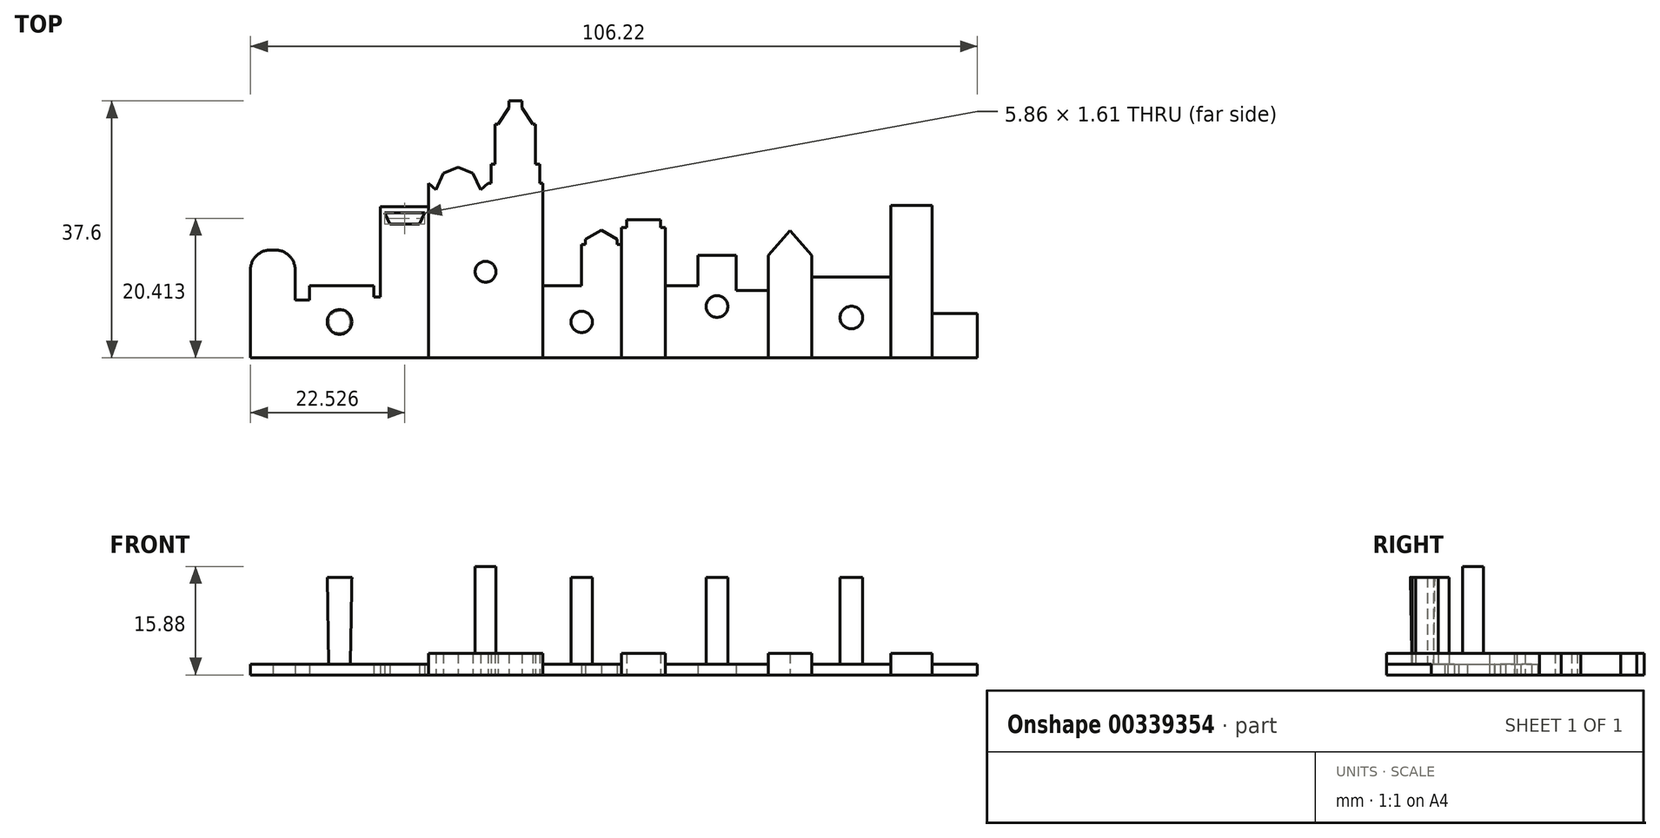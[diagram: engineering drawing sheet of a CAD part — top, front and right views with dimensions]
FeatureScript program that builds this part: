
annotation { "Feature Type Name" : "Feature", "Feature Type Description" : "" }
export const myFeature = defineFeature(function(context is Context, id is Id, definition is map)
    precondition{}
    {
        {
            var Q0;
            Q0=qCreatedBy(makeId("Top.planeOp"),FACE);
            var sketch = newSketch(context, id + "F0", { "sketchPlane" : qUnion([Q0])});
            skLineSegment(sketch, "E0.bottom", {"start": v(0, 0) * mm, "end": v(6.51, 0) * mm});
            skLineSegment(sketch, "E0.top", {"start": v(2.85, 12.93) * mm, "end": v(3.26, 12.93) * mm});
            skLineSegment(sketch, "E0.left", {"start": v(0, 0) * mm, "end": v(0, 12.93) * mm});
            skLineSegment(sketch, "E0.right", {"start": v(6.51, 8.46) * mm, "end": v(6.51, 12.93) * mm});
            skLineSegment(sketch, "E1.bottom", {"start": v(5.34, 0) * mm, "end": v(8.63, 0) * mm});
            skLineSegment(sketch, "E1.top", {"start": v(6.51, 8.46) * mm, "end": v(8.63, 8.46) * mm});
            skLineSegment(sketch, "E2.bottom", {"start": v(8.63, 0) * mm, "end": v(18.03, 0) * mm});
            skLineSegment(sketch, "E2.top", {"start": v(8.63, 10.55) * mm, "end": v(18.03, 10.55) * mm});
            skLineSegment(sketch, "E2.left", {"start": v(8.63, 8.46) * mm, "end": v(8.63, 10.55) * mm});
            skLineSegment(sketch, "E2.right", {"start": v(18.03, 8.93) * mm, "end": v(18.03, 10.55) * mm});
            skLineSegment(sketch, "E3.bottom", {"start": v(16.62, 0) * mm, "end": v(18.97, 0) * mm});
            skLineSegment(sketch, "E3.top", {"start": v(18.03, 8.93) * mm, "end": v(18.97, 8.93) * mm});
            skLineSegment(sketch, "E4.bottom", {"start": v(18.97, 0) * mm, "end": v(26.02, 0) * mm});
            skLineSegment(sketch, "E4.top", {"start": v(18.97, 22.1) * mm, "end": v(26.02, 22.1) * mm});
            skLineSegment(sketch, "E4.left", {"start": v(18.97, 8.93) * mm, "end": v(18.97, 22.1) * mm});
            skLineSegment(sketch, "E4.right", {"start": v(26.02, 0) * mm, "end": v(26.02, 22.1) * mm});
            skLineSegment(sketch, "E5.bottom", {"start": v(26.02, 0) * mm, "end": v(34.71, 0) * mm});
            skLineSegment(sketch, "E5.left", {"start": v(26.02, 0) * mm, "end": v(26.02, 25.53) * mm});
            skLineSegment(sketch, "E5.right", {"start": v(34.71, 0) * mm, "end": v(34.71, 25.53) * mm});
            skLineSegment(sketch, "E6.bottom", {"start": v(34.71, 0) * mm, "end": v(42.7, 0) * mm});
            skLineSegment(sketch, "E6.top", {"start": v(37.76, 37.6) * mm, "end": v(39.65, 37.6) * mm});
            skLineSegment(sketch, "E6.right", {"start": v(42.7, 0) * mm, "end": v(42.7, 25.53) * mm});
            skLineSegment(sketch, "E7.bottom", {"start": v(42.7, 10.55) * mm, "end": v(48.34, 10.55) * mm});
            skLineSegment(sketch, "E7.top", {"start": v(42.7, 0) * mm, "end": v(48.34, 0) * mm});
            skLineSegment(sketch, "E7.left", {"start": v(42.7, 10.55) * mm, "end": v(42.7, 0) * mm});
            skLineSegment(sketch, "E7.right", {"start": v(48.34, 10.55) * mm, "end": v(48.34, 0) * mm});
            skLineSegment(sketch, "E8.bottom", {"start": v(48.34, 0) * mm, "end": v(54.22, 0) * mm});
            skLineSegment(sketch, "E8.left", {"start": v(48.34, 0) * mm, "end": v(48.34, 15.04) * mm});
            skLineSegment(sketch, "E8.right", {"start": v(54.22, 0) * mm, "end": v(54.22, 15.04) * mm});
            skLineSegment(sketch, "E9.top", {"start": v(54.97, 20.21) * mm, "end": v(59.9, 20.21) * mm});
            skLineSegment(sketch, "E9.left", {"start": v(54.22, 15.04) * mm, "end": v(54.22, 19.05) * mm});
            skLineSegment(sketch, "E9.right", {"start": v(60.66, 15.04) * mm, "end": v(60.66, 19.05) * mm});
            skLineSegment(sketch, "E10.top", {"start": v(60.66, 0) * mm, "end": v(54.22, 0) * mm});
            skLineSegment(sketch, "E10.left", {"start": v(60.66, 15.04) * mm, "end": v(60.66, 0) * mm});
            skLineSegment(sketch, "E10.right", {"start": v(54.22, 15.04) * mm, "end": v(54.22, 0) * mm});
            skLineSegment(sketch, "E11.bottom", {"start": v(60.66, 10.55) * mm, "end": v(65.36, 10.55) * mm});
            skLineSegment(sketch, "E11.top", {"start": v(60.66, 0) * mm, "end": v(65.36, 0) * mm});
            skLineSegment(sketch, "E11.left", {"start": v(60.66, 10.55) * mm, "end": v(60.66, 0) * mm});
            skLineSegment(sketch, "E11.right", {"start": v(65.36, 10.55) * mm, "end": v(65.36, 0) * mm});
            skLineSegment(sketch, "E12.bottom", {"start": v(65.36, 0) * mm, "end": v(71, 0) * mm});
            skLineSegment(sketch, "E12.top", {"start": v(65.36, 15.04) * mm, "end": v(71, 15.04) * mm});
            skLineSegment(sketch, "E12.left", {"start": v(65.36, 0) * mm, "end": v(65.36, 15.04) * mm});
            skLineSegment(sketch, "E12.right", {"start": v(71, 0) * mm, "end": v(71, 15.04) * mm});
            skLineSegment(sketch, "E13.bottom", {"start": v(71, 9.87) * mm, "end": v(75.7, 9.87) * mm});
            skLineSegment(sketch, "E13.top", {"start": v(71, 0) * mm, "end": v(75.7, 0) * mm});
            skLineSegment(sketch, "E13.left", {"start": v(71, 9.87) * mm, "end": v(71, 0) * mm});
            skLineSegment(sketch, "E13.right", {"start": v(75.7, 9.87) * mm, "end": v(75.7, 0) * mm});
            skLineSegment(sketch, "E14.bottom", {"start": v(75.7, 0) * mm, "end": v(82.05, 0) * mm});
            skLineSegment(sketch, "E14.left", {"start": v(75.7, 0) * mm, "end": v(75.7, 15.04) * mm});
            skLineSegment(sketch, "E14.right", {"start": v(82.05, 0) * mm, "end": v(82.05, 15.04) * mm});
            skArc(sketch, "E15", {"start": v(3.26, 15.75) * mm, "mid": v(0.98, 15.08) * mm, "end": v(0, 12.93) * mm});
            skPoint(sketch, "E15.startSnap0", {"position": v(3.26, 12.93) * mm});
            skArc(sketch, "E16", {"start": v(6.51, 12.93) * mm, "mid": v(5.53, 15.08) * mm, "end": v(3.26, 15.75) * mm});
            skLineSegment(sketch, "E17", {"start": v(26.02, 25.53) * mm, "end": v(27.1, 24.59) * mm});
            skLineSegment(sketch, "E18", {"start": v(27.1, 24.59) * mm, "end": v(28.2, 27.03) * mm});
            skLineSegment(sketch, "E19", {"start": v(30.37, 27.88) * mm, "end": v(28.2, 27.03) * mm});
            skLineSegment(sketch, "E20.MirrorCS", {"start": v(33.64, 24.59) * mm, "end": v(32.52, 27.03) * mm});
            skLineSegment(sketch, "E21.MirrorCS", {"start": v(30.37, 27.88) * mm, "end": v(32.52, 27.03) * mm});
            skLineSegment(sketch, "E22.MirrorCS", {"start": v(34.71, 25.53) * mm, "end": v(33.64, 24.59) * mm});
            skLineSegment(sketch, "E23", {"start": v(34.71, 25.53) * mm, "end": v(35.16, 25.53) * mm});
            skLineSegment(sketch, "E24", {"start": v(35.16, 25.53) * mm, "end": v(35.16, 28.35) * mm});
            skLineSegment(sketch, "E25", {"start": v(35.16, 28.35) * mm, "end": v(35.75, 28.35) * mm});
            skLineSegment(sketch, "E26", {"start": v(35.75, 28.35) * mm, "end": v(35.75, 34.2) * mm});
            skLineSegment(sketch, "E27", {"start": v(35.75, 34.2) * mm, "end": v(36.17, 34.2) * mm});
            skLineSegment(sketch, "E28", {"start": v(38.7, 37.6) * mm, "end": v(37.76, 37.6) * mm});
            skLineSegment(sketch, "E29", {"start": v(37.76, 37.6) * mm, "end": v(37.76, 36.57) * mm});
            skLineSegment(sketch, "E30", {"start": v(37.76, 36.57) * mm, "end": v(36.17, 34.2) * mm});
            skLineSegment(sketch, "E31.MirrorCS", {"start": v(39.65, 37.6) * mm, "end": v(39.65, 36.57) * mm});
            skLineSegment(sketch, "E32.MirrorCS", {"start": v(39.65, 36.57) * mm, "end": v(41.25, 34.2) * mm});
            skLineSegment(sketch, "E33.MirrorCS", {"start": v(41.66, 34.2) * mm, "end": v(41.25, 34.2) * mm});
            skLineSegment(sketch, "E34.MirrorCS", {"start": v(41.66, 28.35) * mm, "end": v(41.66, 34.2) * mm});
            skLineSegment(sketch, "E35.MirrorCS", {"start": v(42.26, 28.35) * mm, "end": v(41.66, 28.35) * mm});
            skLineSegment(sketch, "E36.MirrorCS", {"start": v(42.26, 25.53) * mm, "end": v(42.26, 28.35) * mm});
            skLineSegment(sketch, "E37.MirrorCS", {"start": v(42.7, 25.53) * mm, "end": v(42.26, 25.53) * mm});
            skLineSegment(sketch, "E38", {"start": v(51.27, 18.7) * mm, "end": v(48.96, 17.37) * mm});
            skLineSegment(sketch, "E39.MirrorCS", {"start": v(51.27, 18.7) * mm, "end": v(53.58, 17.37) * mm});
            skLineSegment(sketch, "E40", {"start": v(48.96, 17.37) * mm, "end": v(48.96, 16.6) * mm});
            skLineSegment(sketch, "E41.MirrorCS", {"start": v(53.58, 17.37) * mm, "end": v(53.58, 16.6) * mm});
            skLineSegment(sketch, "E42", {"start": v(48.96, 16.6) * mm, "end": v(48.34, 16.6) * mm});
            skLineSegment(sketch, "E43", {"start": v(48.34, 15.04) * mm, "end": v(48.34, 16.6) * mm});
            skLineSegment(sketch, "E44.MirrorCS", {"start": v(53.58, 16.6) * mm, "end": v(54.2, 16.6) * mm});
            skLineSegment(sketch, "E45.MirrorCS", {"start": v(54.2, 15.04) * mm, "end": v(54.2, 16.6) * mm});
            skLineSegment(sketch, "E46.top", {"start": v(54.22, 19.05) * mm, "end": v(54.97, 19.05) * mm});
            skLineSegment(sketch, "E47.right", {"start": v(54.97, 20.21) * mm, "end": v(54.97, 19.05) * mm});
            skLineSegment(sketch, "E48.MirrorCS", {"start": v(59.9, 20.21) * mm, "end": v(59.9, 19.05) * mm});
            skLineSegment(sketch, "E49", {"start": v(78.87, 18.62) * mm, "end": v(75.7, 15.04) * mm});
            skLineSegment(sketch, "E50", {"start": v(78.87, 18.62) * mm, "end": v(82.05, 15.04) * mm});
            skLineSegment(sketch, "E51.bottom", {"start": v(82.05, 0) * mm, "end": v(93.6, 0) * mm});
            skLineSegment(sketch, "E51.top", {"start": v(82.05, 11.81) * mm, "end": v(93.6, 11.81) * mm});
            skLineSegment(sketch, "E51.left", {"start": v(82.05, 0) * mm, "end": v(82.05, 11.81) * mm});
            skLineSegment(sketch, "E51.right", {"start": v(93.6, 0) * mm, "end": v(93.6, 11.81) * mm});
            skLineSegment(sketch, "E52.bottom", {"start": v(93.6, 0) * mm, "end": v(99.63, 0) * mm});
            skLineSegment(sketch, "E52.top", {"start": v(93.6, 22.32) * mm, "end": v(99.63, 22.32) * mm});
            skLineSegment(sketch, "E52.left", {"start": v(93.6, 0) * mm, "end": v(93.6, 22.32) * mm});
            skLineSegment(sketch, "E52.right", {"start": v(99.63, 0) * mm, "end": v(99.63, 22.32) * mm});
            skLineSegment(sketch, "E53.bottom", {"start": v(99.63, 0) * mm, "end": v(106.22, 0) * mm});
            skLineSegment(sketch, "E53.top", {"start": v(99.63, 6.5) * mm, "end": v(106.22, 6.5) * mm});
            skLineSegment(sketch, "E53.left", {"start": v(99.63, 0) * mm, "end": v(99.63, 6.5) * mm});
            skLineSegment(sketch, "E53.right", {"start": v(106.22, 0) * mm, "end": v(106.22, 6.5) * mm});
            skPoint(sketch, "E54.MirrorCS.end.orphan", {"position": v(51.27, 15.04) * mm});
            skLineSegment(sketch, "E55.trimOffspring", {"start": v(54.2, 15.04) * mm, "end": v(54.22, 15.04) * mm});
            skLineSegment(sketch, "E56.trimOffspring", {"start": v(59.9, 19.05) * mm, "end": v(60.66, 19.05) * mm});
            skPoint(sketch, "E10.bottom.end.orphan", {"position": v(59.9, 15.04) * mm});
            skPoint(sketch, "E57.trimOffspring.start.orphan", {"position": v(54.97, 15.04) * mm});
            skPoint(sketch, "E14.top.start.orphan", {"position": v(78.87, 15.04) * mm});
            skLineSegment(sketch, "E58", {"start": v(19.6, 21.22) * mm, "end": v(25.46, 21.22) * mm});
            skLineSegment(sketch, "E59", {"start": v(25.46, 21.22) * mm, "end": v(24.69, 19.61) * mm});
            skLineSegment(sketch, "E60.MirrorCS", {"start": v(19.6, 21.22) * mm, "end": v(20.36, 19.61) * mm});
            skLineSegment(sketch, "E61", {"start": v(20.36, 19.61) * mm, "end": v(24.69, 19.61) * mm});
            skPoint(sketch, "E62.orphan", {"position": v(22.53, 21.22) * mm});
            skSolve(sketch);
        }
        {
            var Q0;
            Q0=makeQuery(id+"F0.imprint","IMPRINT",FACE,{"disambiguationData":[TD([[makeQuery(id+"F0.imprint","IMPRINT",EDGE,{"derivedFrom":sQuery(id+"F0.wireOp",EDGE,"E6.bottom")}),1.0]])]});
            var Q1;
            {var subQ3=sQuery(id+"F0.wireOp",EDGE,"E5.bottom");Q1=makeQuery(id+"F0.imprint","IMPRINT",FACE,{"disambiguationData":[TD([[makeQuery(id+"F0.imprint","IMPRINT",EDGE,{"derivedFrom":subQ3}),1.0]])]});}
            var Q2;
            {var subQ3=sQuery(id+"F0.wireOp",EDGE,"E14.bottom");Q2=makeQuery(id+"F0.imprint","IMPRINT",FACE,{"disambiguationData":[TD([[makeQuery(id+"F0.imprint","IMPRINT",EDGE,{"derivedFrom":subQ3}),1.0]])]});}
            var Q3;
            {var subQ3=sQuery(id+"F0.wireOp",EDGE,"E52.bottom");Q3=makeQuery(id+"F0.imprint","IMPRINT",FACE,{"disambiguationData":[TD([[makeQuery(id+"F0.imprint","IMPRINT",EDGE,{"derivedFrom":subQ3}),1.0]])]});}
            var Q4;
            Q4=makeQuery(id+"F0.imprint","IMPRINT",FACE,{"disambiguationData":[TD([[makeQuery(id+"F0.imprint","IMPRINT",EDGE,{"derivedFrom":sQuery(id+"F0.wireOp",EDGE,"E9.top")}),-1.0]])]});
            extrude(context, id + "F1", {"entities" : qUnion([Q0, Q1, Q2, Q3, Q4]), "depth" : 3.17 * mm});
        }
        {
            var Q0;
            {var subQ3=sQuery(id+"F0.wireOp",EDGE,"E0.bottom");Q0=makeQuery(id+"F0.imprint","IMPRINT",FACE,{"disambiguationData":[TD([[makeQuery(id+"F0.imprint","IMPRINT",EDGE,{"derivedFrom":subQ3}),1.0]])]});}
            var Q1;
            {var subQ0=sQuery(id+"F0.wireOp",EDGE,"E7.bottom");Q1=makeQuery(id+"F0.imprint","IMPRINT",FACE,{"disambiguationData":[TD([[makeQuery(id+"F0.imprint","IMPRINT",EDGE,{"derivedFrom":subQ0}),-1.0]])]});}
            var Q2;
            {var subQ3=sQuery(id+"F0.wireOp",EDGE,"E8.bottom");Q2=makeQuery(id+"F0.imprint","IMPRINT",FACE,{"disambiguationData":[TD([[makeQuery(id+"F0.imprint","IMPRINT",EDGE,{"derivedFrom":subQ3}),1.0]])]});}
            var Q3;
            {var subQ3=sQuery(id+"F0.wireOp",EDGE,"E12.bottom");Q3=makeQuery(id+"F0.imprint","IMPRINT",FACE,{"disambiguationData":[TD([[makeQuery(id+"F0.imprint","IMPRINT",EDGE,{"derivedFrom":subQ3}),1.0]])]});}
            var Q4;
            {var subQ0=sQuery(id+"F0.wireOp",EDGE,"E51.bottom");Q4=makeQuery(id+"F0.imprint","IMPRINT",FACE,{"disambiguationData":[TD([[makeQuery(id+"F0.imprint","IMPRINT",EDGE,{"derivedFrom":subQ0}),1.0]])]});}
            var Q5;
            Q5=makeQuery(id+"F0.imprint","IMPRINT",FACE,{"disambiguationData":[TD([[makeQuery(id+"F0.imprint","IMPRINT",EDGE,{"derivedFrom":sQuery(id+"F0.wireOp",EDGE,"E53.bottom")}),1.0]])]});
            var Q6;
            {var subQ0=sQuery(id+"F0.wireOp",EDGE,"E11.bottom");Q6=makeQuery(id+"F0.imprint","IMPRINT",FACE,{"disambiguationData":[TD([[makeQuery(id+"F0.imprint","IMPRINT",EDGE,{"derivedFrom":subQ0}),-1.0]])]});}
            var Q7;
            {var subQ0=sQuery(id+"F0.wireOp",EDGE,"E13.bottom");Q7=makeQuery(id+"F0.imprint","IMPRINT",FACE,{"disambiguationData":[TD([[makeQuery(id+"F0.imprint","IMPRINT",EDGE,{"derivedFrom":subQ0}),-1.0]])]});}
            extrude(context, id + "F2", {"entities" : qUnion([Q0, Q1, Q2, Q3, Q4, Q5, Q6, Q7]), "depth" : 1.59 * mm});
        }
        {
            var Q0;
            Q0=makeQuery(id+"F2.opExtrude","CAP_FACE",FACE,{"disambiguationData":[OSD([sQuery(id+"F0.wireOp",EDGE,"E0.bottom"),sQuery(id+"F0.wireOp",EDGE,"E0.left"),sQuery(id+"F0.wireOp",EDGE,"E0.right"),sQuery(id+"F0.wireOp",EDGE,"E1.bottom"),sQuery(id+"F0.wireOp",EDGE,"E1.top"),sQuery(id+"F0.wireOp",EDGE,"E2.bottom"),sQuery(id+"F0.wireOp",EDGE,"E2.top"),sQuery(id+"F0.wireOp",EDGE,"E2.left"),sQuery(id+"F0.wireOp",EDGE,"E2.right"),sQuery(id+"F0.wireOp",EDGE,"E3.bottom"),sQuery(id+"F0.wireOp",EDGE,"E3.top"),sQuery(id+"F0.wireOp",EDGE,"E4.bottom"),sQuery(id+"F0.wireOp",EDGE,"E4.top"),sQuery(id+"F0.wireOp",EDGE,"E4.left"),sQuery(id+"F0.wireOp",EDGE,"E5.left"),sQuery(id+"F0.wireOp",EDGE,"E15"),sQuery(id+"F0.wireOp",EDGE,"E16"),sQuery(id+"F0.wireOp",EDGE,"E58"),sQuery(id+"F0.wireOp",EDGE,"E59"),sQuery(id+"F0.wireOp",EDGE,"E60.MirrorCS"),sQuery(id+"F0.wireOp",EDGE,"E61")])],"isStart":false});
            var sketch = newSketch(context, id + "F3", { "sketchPlane" : qUnion([Q0])});
            skLineSegment(sketch, "E63", {"start": v(13, 0) * mm, "end": v(13, 3.69) * mm});
            skCircle(sketch, "E64", {"center": v(13, 5.27) * mm, "radius": 1.58 * mm});
            skLineSegment(sketch, "E65.trimOffspring", {"start": v(13, 6.86) * mm, "end": v(13, 10.55) * mm});
            skSolve(sketch);
        }
        {
            var Q0;
            Q0=makeQuery(id+"F1.opExtrude","CAP_FACE",FACE,{"disambiguationData":[OSD([sQuery(id+"F0.wireOp",EDGE,"E5.bottom"),sQuery(id+"F0.wireOp",EDGE,"E5.left"),sQuery(id+"F0.wireOp",EDGE,"E6.bottom"),sQuery(id+"F0.wireOp",EDGE,"E6.top"),sQuery(id+"F0.wireOp",EDGE,"E6.right"),sQuery(id+"F0.wireOp",EDGE,"E7.left"),sQuery(id+"F0.wireOp",EDGE,"E17"),sQuery(id+"F0.wireOp",EDGE,"E18"),sQuery(id+"F0.wireOp",EDGE,"E19"),sQuery(id+"F0.wireOp",EDGE,"E20.MirrorCS"),sQuery(id+"F0.wireOp",EDGE,"E21.MirrorCS"),sQuery(id+"F0.wireOp",EDGE,"E22.MirrorCS"),sQuery(id+"F0.wireOp",EDGE,"E23"),sQuery(id+"F0.wireOp",EDGE,"E24"),sQuery(id+"F0.wireOp",EDGE,"E25"),sQuery(id+"F0.wireOp",EDGE,"E26"),sQuery(id+"F0.wireOp",EDGE,"E27"),sQuery(id+"F0.wireOp",EDGE,"E28"),sQuery(id+"F0.wireOp",EDGE,"E29"),sQuery(id+"F0.wireOp",EDGE,"E30"),sQuery(id+"F0.wireOp",EDGE,"E31.MirrorCS"),sQuery(id+"F0.wireOp",EDGE,"E32.MirrorCS"),sQuery(id+"F0.wireOp",EDGE,"E33.MirrorCS"),sQuery(id+"F0.wireOp",EDGE,"E34.MirrorCS"),sQuery(id+"F0.wireOp",EDGE,"E35.MirrorCS"),sQuery(id+"F0.wireOp",EDGE,"E36.MirrorCS"),sQuery(id+"F0.wireOp",EDGE,"E37.MirrorCS")])],"isStart":false});
            var sketch = newSketch(context, id + "F4", { "sketchPlane" : qUnion([Q0])});
            skLineSegment(sketch, "E66", {"start": v(34.36, 0) * mm, "end": v(34.36, 11.08) * mm});
            skCircle(sketch, "E67", {"center": v(34.36, 12.6) * mm, "radius": 1.53 * mm});
            skLineSegment(sketch, "E68.trimOffspring", {"start": v(34.36, 14.14) * mm, "end": v(34.36, 25.22) * mm});
            skSolve(sketch);
        }
        {
            var Q0;
            Q0=makeQuery(id+"F2.opExtrude","CAP_FACE",FACE,{"disambiguationData":[OSD([sQuery(id+"F0.wireOp",EDGE,"E7.bottom"),sQuery(id+"F0.wireOp",EDGE,"E7.top"),sQuery(id+"F0.wireOp",EDGE,"E7.left"),sQuery(id+"F0.wireOp",EDGE,"E8.bottom"),sQuery(id+"F0.wireOp",EDGE,"E8.left"),sQuery(id+"F0.wireOp",EDGE,"E10.right"),sQuery(id+"F0.wireOp",EDGE,"E38"),sQuery(id+"F0.wireOp",EDGE,"E39.MirrorCS"),sQuery(id+"F0.wireOp",EDGE,"E40"),sQuery(id+"F0.wireOp",EDGE,"E41.MirrorCS"),sQuery(id+"F0.wireOp",EDGE,"E42"),sQuery(id+"F0.wireOp",EDGE,"E43"),sQuery(id+"F0.wireOp",EDGE,"E44.MirrorCS"),sQuery(id+"F0.wireOp",EDGE,"E45.MirrorCS"),sQuery(id+"F0.wireOp",EDGE,"E55.trimOffspring")])],"isStart":false});
            var sketch = newSketch(context, id + "F5", { "sketchPlane" : qUnion([Q0])});
            skLineSegment(sketch, "E69", {"start": v(48.46, 0) * mm, "end": v(48.42, 3.7) * mm});
            skCircle(sketch, "E70", {"center": v(48.4, 5.27) * mm, "radius": 1.56 * mm});
            skLineSegment(sketch, "E71.trimOffspring", {"start": v(48.39, 6.84) * mm, "end": v(48.34, 10.55) * mm});
            skSolve(sketch);
        }
        {
            var Q0;
            Q0=makeQuery(id+"F2.opExtrude","CAP_FACE",FACE,{"disambiguationData":[OSD([sQuery(id+"F0.wireOp",EDGE,"E11.bottom"),sQuery(id+"F0.wireOp",EDGE,"E11.top"),sQuery(id+"F0.wireOp",EDGE,"E11.left"),sQuery(id+"F0.wireOp",EDGE,"E12.bottom"),sQuery(id+"F0.wireOp",EDGE,"E12.top"),sQuery(id+"F0.wireOp",EDGE,"E12.left"),sQuery(id+"F0.wireOp",EDGE,"E12.right"),sQuery(id+"F0.wireOp",EDGE,"E13.bottom"),sQuery(id+"F0.wireOp",EDGE,"E13.top"),sQuery(id+"F0.wireOp",EDGE,"E14.left")])],"isStart":false});
            var sketch = newSketch(context, id + "F6", { "sketchPlane" : qUnion([Q0])});
            skLineSegment(sketch, "E72", {"start": v(68.18, 0) * mm, "end": v(68.18, 5.94) * mm});
            skCircle(sketch, "E73", {"center": v(68.18, 7.52) * mm, "radius": 1.59 * mm});
            skLineSegment(sketch, "E74.trimOffspring", {"start": v(68.18, 9.1) * mm, "end": v(68.18, 15.04) * mm});
            skSolve(sketch);
        }
        {
            var Q0;
            Q0=makeQuery(id+"F2.opExtrude","CAP_FACE",FACE,{"disambiguationData":[OSD([sQuery(id+"F0.wireOp",EDGE,"E51.bottom"),sQuery(id+"F0.wireOp",EDGE,"E51.top"),sQuery(id+"F0.wireOp",EDGE,"E51.left"),sQuery(id+"F0.wireOp",EDGE,"E52.left")])],"isStart":false});
            var sketch = newSketch(context, id + "F7", { "sketchPlane" : qUnion([Q0])});
            skLineSegment(sketch, "E75", {"start": v(87.83, 0) * mm, "end": v(87.83, 4.25) * mm});
            skCircle(sketch, "E76", {"center": v(87.83, 5.9) * mm, "radius": 1.65 * mm});
            skLineSegment(sketch, "E77.trimOffspring", {"start": v(87.83, 7.56) * mm, "end": v(87.83, 11.81) * mm});
            skSolve(sketch);
        }
        {
            var Q0;
            {var subQ0=sQuery(id+"F3.wireOp",EDGE,"E64");var subQ1=makeQuery(id+"F3.imprint","INTERSECT",VERTEX,{"derivedFrom":[sQuery(id+"F3.wireOp",EDGE,"E63"),subQ0]});Q0=makeQuery(id+"F3.imprint","IMPRINT",FACE,{"disambiguationData":[TD([[makeQuery(id+"F3.imprint","IMPRINT",EDGE,{"disambiguationData":[TD([[subQ1,1.0]])],"derivedFrom":subQ0}),1.0]])]});}
            extrude(context, id + "F8", {"entities" : qUnion([Q0]), "operationType" : NewBodyOperationType.ADD, "depth" : 12.7 * mm, "hasDraft" : true, "draftAngle" : 1 * degree});
        }
        {
            var Q0;
            {var subQ0=sQuery(id+"F4.wireOp",EDGE,"E67");var subQ1=makeQuery(id+"F4.imprint","INTERSECT",VERTEX,{"derivedFrom":[sQuery(id+"F4.wireOp",EDGE,"E66"),subQ0]});Q0=makeQuery(id+"F4.imprint","IMPRINT",FACE,{"disambiguationData":[TD([[makeQuery(id+"F4.imprint","IMPRINT",EDGE,{"disambiguationData":[TD([[subQ1,1.0]])],"derivedFrom":subQ0}),1.0]])]});}
            var Q1;
            {var subQ0=sQuery(id+"F5.wireOp",EDGE,"E70");var subQ1=makeQuery(id+"F5.imprint","INTERSECT",VERTEX,{"derivedFrom":[sQuery(id+"F5.wireOp",EDGE,"E69"),subQ0]});Q1=makeQuery(id+"F5.imprint","IMPRINT",FACE,{"disambiguationData":[TD([[makeQuery(id+"F5.imprint","IMPRINT",EDGE,{"disambiguationData":[TD([[subQ1,1.0]])],"derivedFrom":subQ0}),1.0]])]});}
            var Q2;
            {var subQ0=sQuery(id+"F6.wireOp",EDGE,"E73");var subQ1=makeQuery(id+"F6.imprint","INTERSECT",VERTEX,{"derivedFrom":[sQuery(id+"F6.wireOp",EDGE,"E72"),subQ0]});Q2=makeQuery(id+"F6.imprint","IMPRINT",FACE,{"disambiguationData":[TD([[makeQuery(id+"F6.imprint","IMPRINT",EDGE,{"disambiguationData":[TD([[subQ1,1.0]])],"derivedFrom":subQ0}),1.0]])]});}
            var Q3;
            {var subQ0=sQuery(id+"F7.wireOp",EDGE,"E76");var subQ1=makeQuery(id+"F7.imprint","INTERSECT",VERTEX,{"derivedFrom":[sQuery(id+"F7.wireOp",EDGE,"E75"),subQ0]});Q3=makeQuery(id+"F7.imprint","IMPRINT",FACE,{"disambiguationData":[TD([[makeQuery(id+"F7.imprint","IMPRINT",EDGE,{"disambiguationData":[TD([[subQ1,1.0]])],"derivedFrom":subQ0}),1.0]])]});}
            extrude(context, id + "F9", {"entities" : qUnion([Q0, Q1, Q2, Q3]), "depth" : 12.7 * mm});
        }
    });
